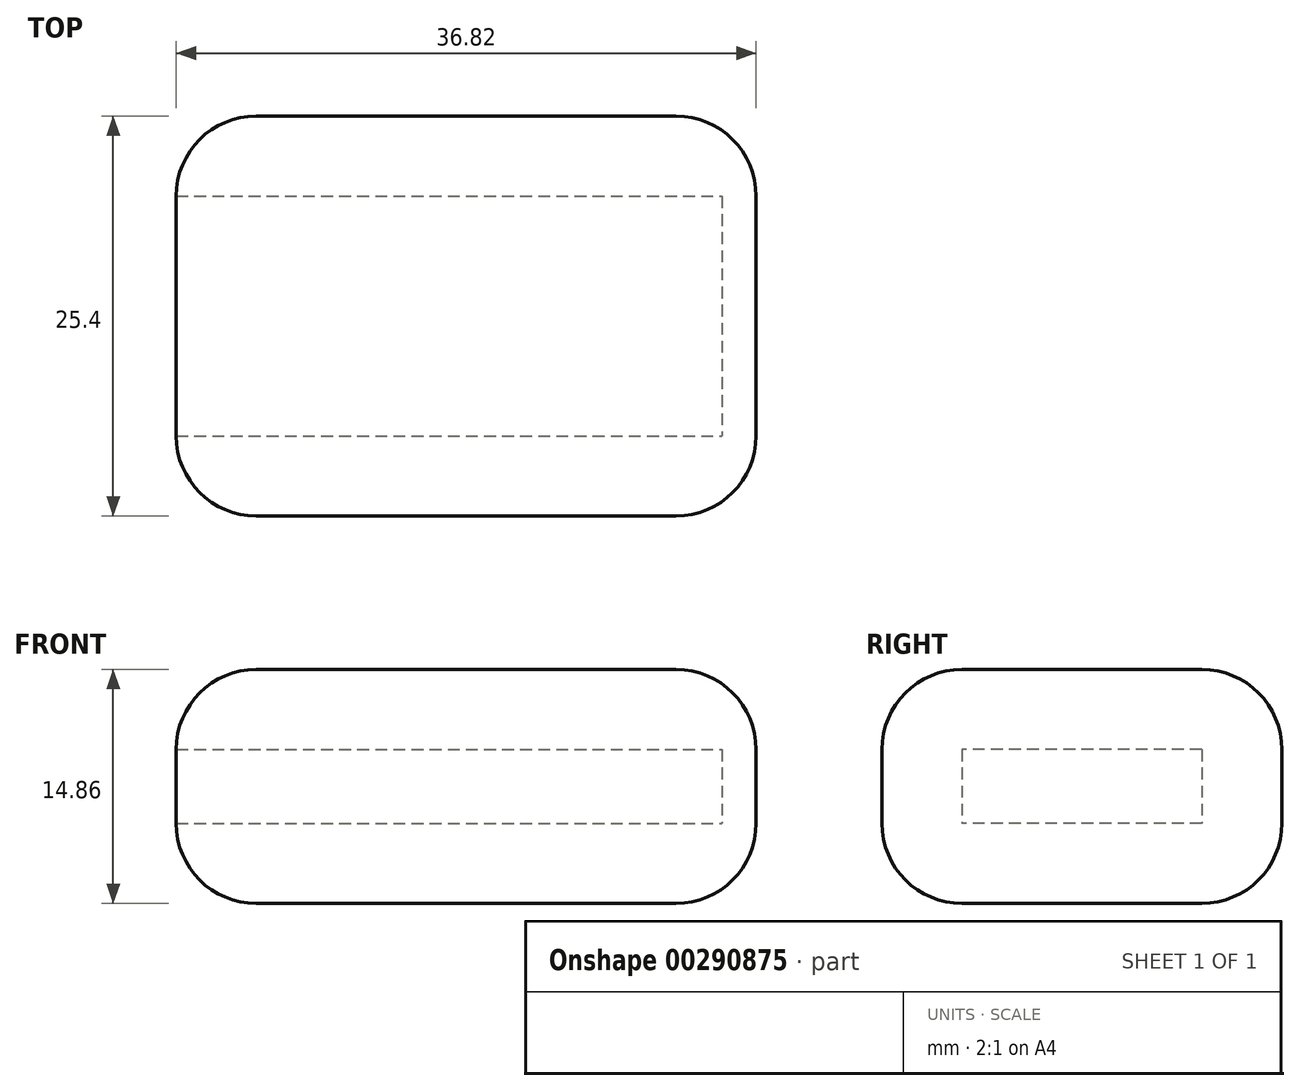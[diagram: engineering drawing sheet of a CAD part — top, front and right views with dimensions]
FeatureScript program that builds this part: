
annotation { "Feature Type Name" : "Feature", "Feature Type Description" : "" }
export const myFeature = defineFeature(function(context is Context, id is Id, definition is map)
    precondition{}
    {
        {
            var Q0;
            Q0=qCreatedBy(makeId("Top.planeOp"),FACE);
            var sketch = newSketch(context, id + "F0", { "sketchPlane" : qUnion([Q0])});
            skLineSegment(sketch, "E0.bottom", {"start": v(18.41, 12.7) * mm, "end": v(-18.41, 12.7) * mm});
            skLineSegment(sketch, "E0.top", {"start": v(18.41, -12.7) * mm, "end": v(-18.41, -12.7) * mm});
            skLineSegment(sketch, "E0.left", {"start": v(18.41, 12.7) * mm, "end": v(18.41, -12.7) * mm});
            skLineSegment(sketch, "E0.right", {"start": v(-18.41, 12.7) * mm, "end": v(-18.41, -12.7) * mm});
            skPoint(sketch, "E0.middle", {"position": v(0, 0) * mm});
            skSolve(sketch);
        }
        {
            var Q0;
            Q0 = qSketchRegion(id + "F0", true);
            extrude(context, id + "F1", {"entities" : qUnion([Q0]), "depth" : 14.86 * mm});
        }
        {
            var Q0;
            Q0=qCreatedBy(makeId("Right.planeOp"),FACE);
            var sketch = newSketch(context, id + "F2", { "sketchPlane" : qUnion([Q0])});
            skLineSegment(sketch, "E1", {"start": v(0, 0) * mm, "end": v(0, 14.86) * mm, "construction": true});
            skLineSegment(sketch, "E2", {"start": v(0, 0) * mm, "end": v(0, 7.43) * mm, "construction": true});
            skLineSegment(sketch, "E3.bottom", {"start": v(7.62, 9.78) * mm, "end": v(-7.62, 9.78) * mm});
            skLineSegment(sketch, "E3.top", {"start": v(7.62, 5.08) * mm, "end": v(-7.62, 5.08) * mm});
            skLineSegment(sketch, "E3.left", {"start": v(7.62, 9.78) * mm, "end": v(7.62, 5.08) * mm});
            skLineSegment(sketch, "E3.right", {"start": v(-7.62, 9.78) * mm, "end": v(-7.62, 5.08) * mm});
            skPoint(sketch, "E3.middle", {"position": v(0, 7.43) * mm});
            skSolve(sketch);
        }
        {
            var Q0;
            Q0 = qSketchRegion(id + "F2", true);
            extrude(context, id + "F3", {"entities" : qUnion([Q0]), "operationType" : NewBodyOperationType.REMOVE, "oppositeDirection" : true, "depth" : 18.54 * mm});
        }
        {
            var Q0;
            Q0 = qSketchRegion(id + "F2", true);
            extrude(context, id + "F4", {"entities" : qUnion([Q0]), "operationType" : NewBodyOperationType.REMOVE, "depth" : 16.26 * mm});
        }
        {
            var Q0;
            Q0=makeQuery(id+"F1.opExtrude","CAP_EDGE",EDGE,{"disambiguationData":[OSD([sQuery(id+"F0.wireOp",EDGE,"E0.top")])],"isStart":false});
            var Q1;
            Q1=makeQuery(id+"F1.opExtrude","CAP_EDGE",EDGE,{"disambiguationData":[OSD([sQuery(id+"F0.wireOp",EDGE,"E0.left")])],"isStart":false});
            var Q2;
            Q2=makeQuery(id+"F1.opExtrude","SWEPT_EDGE",EDGE,{"disambiguationData":[OSD([sQuery(id+"F0.wireOp",EDGE,"E0.top"),sQuery(id+"F0.wireOp",EDGE,"E0.left")])]});
            var Q3;
            Q3=makeQuery(id+"F1.opExtrude","CAP_EDGE",EDGE,{"disambiguationData":[OSD([sQuery(id+"F0.wireOp",EDGE,"E0.left")])],"isStart":true});
            var Q4;
            Q4=makeQuery(id+"F1.opExtrude","SWEPT_EDGE",EDGE,{"disambiguationData":[OSD([sQuery(id+"F0.wireOp",EDGE,"E0.bottom"),sQuery(id+"F0.wireOp",EDGE,"E0.left")])]});
            var Q5;
            Q5=makeQuery(id+"F1.opExtrude","CAP_EDGE",EDGE,{"disambiguationData":[OSD([sQuery(id+"F0.wireOp",EDGE,"E0.bottom")])],"isStart":true});
            var Q6;
            Q6=makeQuery(id+"F1.opExtrude","CAP_EDGE",EDGE,{"disambiguationData":[OSD([sQuery(id+"F0.wireOp",EDGE,"E0.top")])],"isStart":true});
            var Q7;
            Q7=makeQuery(id+"F1.opExtrude","CAP_EDGE",EDGE,{"disambiguationData":[OSD([sQuery(id+"F0.wireOp",EDGE,"E0.bottom")])],"isStart":false});
            var Q8;
            Q8=makeQuery(id+"F1.opExtrude","CAP_EDGE",EDGE,{"disambiguationData":[OSD([sQuery(id+"F0.wireOp",EDGE,"E0.right")])],"isStart":false});
            var Q9;
            Q9=makeQuery(id+"F1.opExtrude","SWEPT_EDGE",EDGE,{"disambiguationData":[OSD([sQuery(id+"F0.wireOp",EDGE,"E0.bottom"),sQuery(id+"F0.wireOp",EDGE,"E0.right")])]});
            var Q10;
            Q10=makeQuery(id+"F1.opExtrude","CAP_EDGE",EDGE,{"disambiguationData":[OSD([sQuery(id+"F0.wireOp",EDGE,"E0.right")])],"isStart":true});
            var Q11;
            Q11=makeQuery(id+"F1.opExtrude","SWEPT_EDGE",EDGE,{"disambiguationData":[OSD([sQuery(id+"F0.wireOp",EDGE,"E0.top"),sQuery(id+"F0.wireOp",EDGE,"E0.right")])]});
            fillet(context, id + "F5", {"entities" : qUnion([Q0, Q1, Q2, Q3, Q4, Q5, Q6, Q7, Q8, Q9, Q10, Q11]), "radius" : 5.08 * mm, "tangentPropagation" : true, "allowEdgeOverflow" : false});
        }
    });
